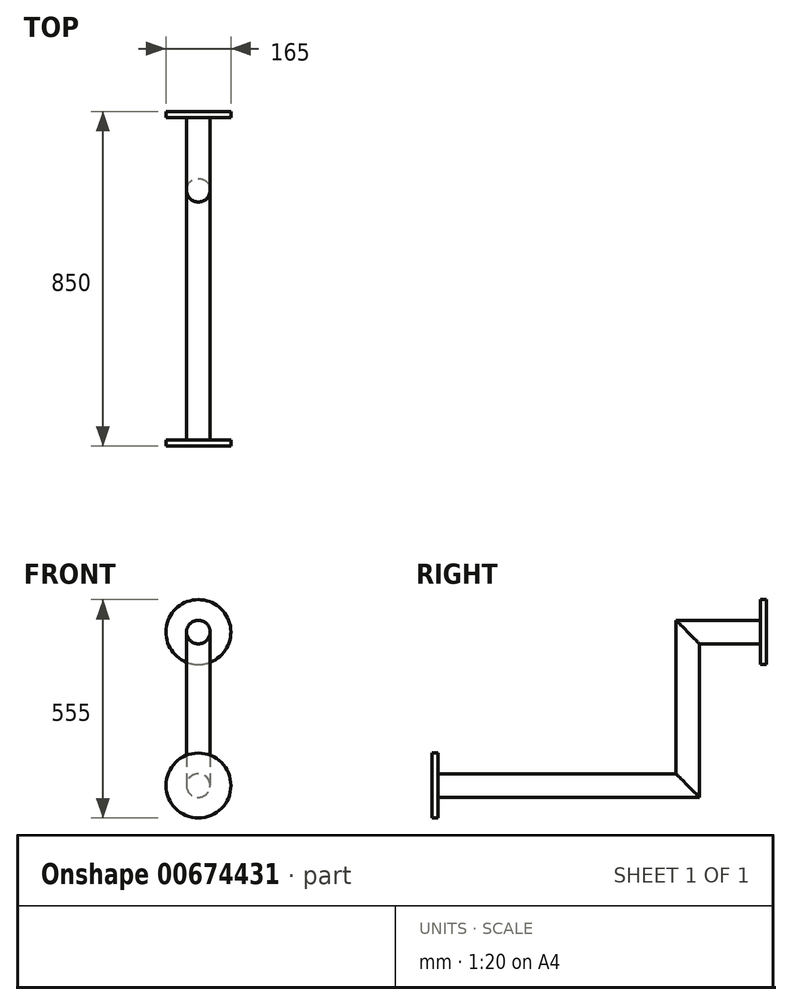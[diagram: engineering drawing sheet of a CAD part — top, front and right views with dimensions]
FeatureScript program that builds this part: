
annotation { "Feature Type Name" : "Feature", "Feature Type Description" : "" }
export const myFeature = defineFeature(function(context is Context, id is Id, definition is map)
    precondition{}
    {
        {
            var Q0;
            Q0=qCreatedBy(makeId("Front.planeOp"),FACE);
            var sketch = newSketch(context, id + "F0", { "sketchPlane" : qUnion([Q0])});
            skCircle(sketch, "E0", {"center": v(0, 0) * mm, "radius": 30 * mm});
            skCircle(sketch, "E1", {"center": v(0, 0) * mm, "radius": 82.5 * mm});
            skSolve(sketch);
        }
        {
            var Q0;
            Q0=qCreatedBy(makeId("Right.planeOp"),FACE);
            var sketch = newSketch(context, id + "F1", { "sketchPlane" : qUnion([Q0])});
            skLineSegment(sketch, "E2", {"start": v(0, 0) * mm, "end": v(-200, 0) * mm});
            skLineSegment(sketch, "E3", {"start": v(-200, 0) * mm, "end": v(-200, -390) * mm});
            skLineSegment(sketch, "E4", {"start": v(-200, -390) * mm, "end": v(-850, -390) * mm});
            skSolve(sketch);
        }
        {
            var Q0;
            Q0=makeQuery(id+"F0.imprint","IMPRINT",FACE,{"disambiguationData":[TD([[makeQuery(id+"F0.imprint","IMPRINT",EDGE,{"derivedFrom":sQuery(id+"F0.wireOp",EDGE,"E0")}),1.0]])]});
            var Q1;
            Q1=sQuery(id+"F0.wireOp",EDGE,"E0");
            var Q2;
            Q2=sQuery(id+"F1.wireOp",EDGE,"E2");
            var Q3;
            Q3=sQuery(id+"F1.wireOp",EDGE,"E3");
            var Q4;
            Q4=sQuery(id+"F1.wireOp",EDGE,"E4");
            sweep(context, id + "F2", {"profiles" : qUnion([Q0]), "surfaceProfiles" : qUnion([Q1]), "path" : qUnion([Q2, Q3, Q4])});
        }
        {
            var Q0;
            Q0=makeQuery(id+"F0.imprint","IMPRINT",FACE,{"disambiguationData":[TD([[makeQuery(id+"F0.imprint","IMPRINT",EDGE,{"derivedFrom":sQuery(id+"F0.wireOp",EDGE,"E0")}),-1.0]])]});
            extrude(context, id + "F3", {"entities" : qUnion([Q0]), "operationType" : NewBodyOperationType.ADD, "depth" : 15 * mm, "offsetDistance" : 25 * mm});
        }
        {
            var Q0;
            Q0=makeQuery(id+"F2.opSweep","CAP_FACE",FACE,{"disambiguationData":[OSD([sQuery(id+"F0.wireOp",EDGE,"E0"),sQuery(id+"F1.wireOp",VERTEX,"E4.end")])],"isStart":false});
            var sketch = newSketch(context, id + "F4", { "sketchPlane" : qUnion([Q0])});
            skCircle(sketch, "E5", {"center": v(0, -390) * mm, "radius": 82.5 * mm});
            skSolve(sketch);
        }
        {
            var Q0;
            Q0=makeQuery(id+"F4.imprint","IMPRINT",FACE,{"disambiguationData":[TD([[makeQuery(id+"F4.imprint","IMPRINT",EDGE,{"derivedFrom":sQuery(id+"F4.wireOp",EDGE,"E5")}),1.0]])]});
            extrude(context, id + "F5", {"entities" : qUnion([Q0]), "operationType" : NewBodyOperationType.ADD, "oppositeDirection" : true, "depth" : 15 * mm, "offsetDistance" : 25 * mm});
        }
    });
